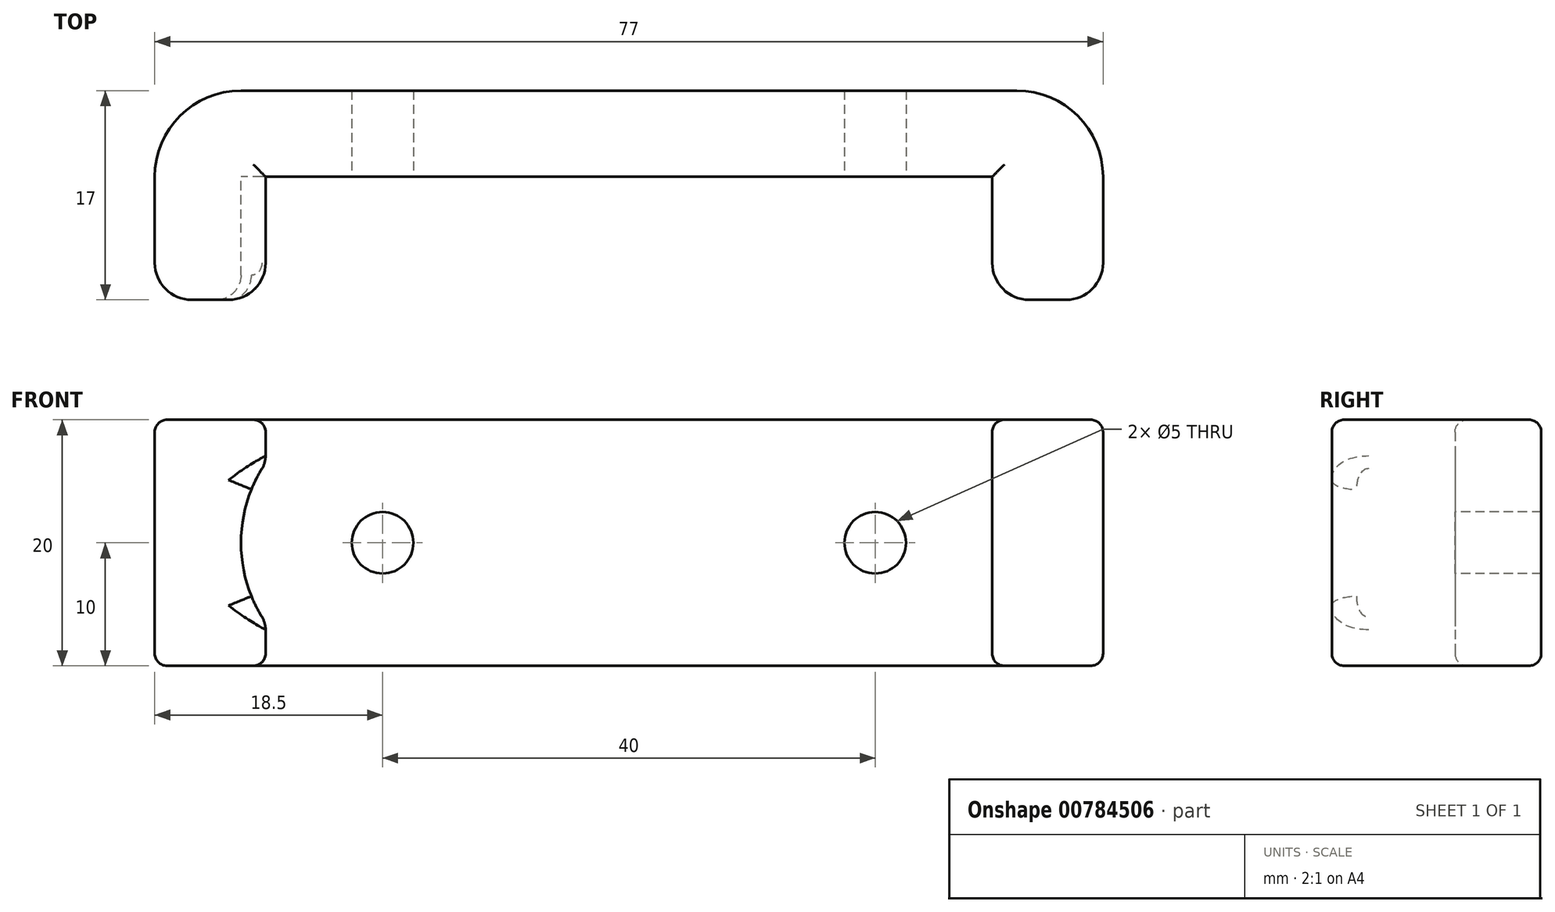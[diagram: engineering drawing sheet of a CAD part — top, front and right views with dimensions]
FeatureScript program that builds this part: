
annotation { "Feature Type Name" : "Feature", "Feature Type Description" : "" }
export const myFeature = defineFeature(function(context is Context, id is Id, definition is map)
    precondition{}
    {
        {
            var Q0;
            Q0=qCreatedBy(makeId("Top.planeOp"),FACE);
            var sketch = newSketch(context, id + "F0", { "sketchPlane" : qUnion([Q0])});
            skLineSegment(sketch, "E0.bottom", {"start": v(-31.5, 3.5) * mm, "end": v(31.5, 3.5) * mm});
            skLineSegment(sketch, "E0.top", {"start": v(-38.5, -3.5) * mm, "end": v(38.5, -3.5) * mm});
            skLineSegment(sketch, "E0.left", {"start": v(-38.5, -3.5) * mm, "end": v(-38.5, -3.5) * mm});
            skLineSegment(sketch, "E0.right", {"start": v(38.5, -3.5) * mm, "end": v(38.5, -3.5) * mm});
            skPoint(sketch, "E0.middle", {"position": v(0, 0) * mm});
            skLineSegment(sketch, "E1.bottom", {"start": v(-38.5, -3.5) * mm, "end": v(-29.5, -3.5) * mm});
            skLineSegment(sketch, "E1.top", {"start": v(-35.5, -13.5) * mm, "end": v(-32.5, -13.5) * mm});
            skLineSegment(sketch, "E1.left", {"start": v(-38.5, -3.5) * mm, "end": v(-38.5, -10.5) * mm});
            skLineSegment(sketch, "E1.right", {"start": v(-29.5, -3.5) * mm, "end": v(-29.5, -10.5) * mm});
            skLineSegment(sketch, "E2.bottom", {"start": v(38.5, -3.5) * mm, "end": v(29.5, -3.5) * mm});
            skLineSegment(sketch, "E2.top", {"start": v(35.5, -13.5) * mm, "end": v(32.5, -13.5) * mm});
            skLineSegment(sketch, "E2.left", {"start": v(38.5, -3.5) * mm, "end": v(38.5, -10.5) * mm});
            skLineSegment(sketch, "E2.right", {"start": v(29.5, -3.5) * mm, "end": v(29.5, -10.5) * mm});
            skCircle(sketch, "E3", {"center": v(0, 0) * mm, "radius": 20 * mm, "construction": true});
            skPoint(sketch, "E4.visualSharp", {"position": v(-38.5, 3.5) * mm});
            skArc(sketch, "E4.filletArc", {"start": v(-31.5, 3.5) * mm, "mid": v(-36.45, 1.45) * mm, "end": v(-38.5, -3.5) * mm});
            skPoint(sketch, "E5.visualSharp", {"position": v(38.5, 3.5) * mm});
            skArc(sketch, "E5.filletArc", {"start": v(38.5, -3.5) * mm, "mid": v(36.45, 1.45) * mm, "end": v(31.5, 3.5) * mm});
            skPoint(sketch, "E6.visualSharp", {"position": v(-38.5, -13.5) * mm});
            skArc(sketch, "E6.filletArc", {"start": v(-38.5, -10.5) * mm, "mid": v(-37.62, -12.62) * mm, "end": v(-35.5, -13.5) * mm});
            skPoint(sketch, "E7.visualSharp", {"position": v(29.5, -13.5) * mm});
            skArc(sketch, "E7.filletArc", {"start": v(29.5, -10.5) * mm, "mid": v(30.38, -12.62) * mm, "end": v(32.5, -13.5) * mm});
            skPoint(sketch, "E8.visualSharp", {"position": v(-29.5, -13.5) * mm});
            skArc(sketch, "E8.filletArc", {"start": v(-32.5, -13.5) * mm, "mid": v(-30.38, -12.62) * mm, "end": v(-29.5, -10.5) * mm});
            skPoint(sketch, "E9.visualSharp", {"position": v(38.5, -13.5) * mm});
            skArc(sketch, "E9.filletArc", {"start": v(35.5, -13.5) * mm, "mid": v(37.62, -12.62) * mm, "end": v(38.5, -10.5) * mm});
            skSolve(sketch);
        }
        {
            var Q0;
            Q0=makeQuery(id+"F0.imprint","IMPRINT",FACE,{"disambiguationData":[TD([[makeQuery(id+"F0.imprint","IMPRINT",EDGE,{"derivedFrom":sQuery(id+"F0.wireOp",EDGE,"E2.top")}),-1.0]])]});
            var Q1;
            Q1=makeQuery(id+"F0.imprint","IMPRINT",FACE,{"disambiguationData":[TD([[makeQuery(id+"F0.imprint","IMPRINT",EDGE,{"derivedFrom":sQuery(id+"F0.wireOp",EDGE,"E0.bottom")}),-1.0]])]});
            var Q2;
            Q2=makeQuery(id+"F0.imprint","IMPRINT",FACE,{"disambiguationData":[TD([[makeQuery(id+"F0.imprint","IMPRINT",EDGE,{"derivedFrom":sQuery(id+"F0.wireOp",EDGE,"E1.top")}),1.0]])]});
            extrude(context, id + "F1", {"entities" : qUnion([Q0, Q1, Q2]), "depth" : 20 * mm, "offsetDistance" : 25 * mm});
        }
        {
            var Q0;
            Q0=makeQuery(id+"F1.opExtrude","SWEPT_FACE",FACE,{"disambiguationData":[OSD([sQuery(id+"F0.wireOp",EDGE,"E0.top")])]});
            var sketch = newSketch(context, id + "F2", { "sketchPlane" : qUnion([Q0])});
            skCircle(sketch, "E10", {"center": v(0, 10) * mm, "radius": 20 * mm, "construction": true});
            skCircle(sketch, "E11", {"center": v(-20, 10) * mm, "radius": 2.5 * mm});
            skCircle(sketch, "E12", {"center": v(20, 10) * mm, "radius": 2.5 * mm});
            skCircle(sketch, "E13", {"center": v(-20, 10) * mm, "radius": 11.5 * mm});
            skCircle(sketch, "E14", {"center": v(20, 10) * mm, "radius": 11.5 * mm});
            skSolve(sketch);
        }
        {
            var Q0;
            Q0=makeQuery(id+"F2.imprint","IMPRINT",FACE,{"disambiguationData":[TD([[makeQuery(id+"F2.imprint","IMPRINT",EDGE,{"derivedFrom":sQuery(id+"F2.wireOp",EDGE,"E11")}),1.0]])]});
            var Q1;
            Q1=makeQuery(id+"F2.imprint","IMPRINT",FACE,{"disambiguationData":[TD([[makeQuery(id+"F2.imprint","IMPRINT",EDGE,{"derivedFrom":sQuery(id+"F2.wireOp",EDGE,"E12")}),1.0]])]});
            extrude(context, id + "F3", {"entities" : qUnion([Q0, Q1]), "operationType" : NewBodyOperationType.REMOVE, "oppositeDirection" : true, "depth" : 7 * mm, "offsetDistance" : 25 * mm});
        }
        {
            var Q0;
            {var subQ0=sQuery(id+"F2.wireOp",EDGE,"E13");var subQ1=makeQuery(id+"F1.opExtrude","SWEPT_EDGE",EDGE,{"disambiguationData":[OSD([sQuery(id+"F0.wireOp",EDGE,"E0.top"),sQuery(id+"F0.wireOp",EDGE,"E1.right")])]});var subQ2=makeQuery(id+"F2.imprint","INTERSECT",VERTEX,{"disambiguationData":[OD(0.0)],"derivedFrom":[subQ1,subQ0]});Q0=makeQuery(id+"F2.imprint","IMPRINT",FACE,{"disambiguationData":[TD([[makeQuery(id+"F2.imprint","IMPRINT",EDGE,{"disambiguationData":[TD([[subQ2,-1.0]])],"derivedFrom":subQ0}),1.0]])]});}
            var Q1;
            {var subQ0=sQuery(id+"F2.wireOp",EDGE,"E14");var subQ1=makeQuery(id+"F1.opExtrude","SWEPT_EDGE",EDGE,{"disambiguationData":[OSD([sQuery(id+"F0.wireOp",EDGE,"E0.top"),sQuery(id+"F0.wireOp",EDGE,"E2.right")])]});var subQ2=makeQuery(id+"F2.imprint","INTERSECT",VERTEX,{"disambiguationData":[OD(0.0)],"derivedFrom":[subQ1,subQ0]});Q1=makeQuery(id+"F2.imprint","IMPRINT",FACE,{"disambiguationData":[TD([[makeQuery(id+"F2.imprint","IMPRINT",EDGE,{"disambiguationData":[TD([[subQ2,1.0]])],"derivedFrom":subQ0}),1.0]])]});}
            var Q2;
            Q2=sQuery(id+"F2.wireOp",EDGE,"E13");
            var Q3;
            Q3=sQuery(id+"F2.wireOp",EDGE,"E14");
            extrude(context, id + "F4", {"entities" : qUnion([Q0, Q1]), "operationType" : NewBodyOperationType.REMOVE, "surfaceEntities" : qUnion([Q2, Q3]), "depth" : 25 * mm, "offsetDistance" : 25 * mm});
        }
        {
            var Q0;
            {var subQ0=sQuery(id+"F2.wireOp",EDGE,"E13");var subQ1=sQuery(id+"F0.wireOp",EDGE,"E1.right");var subQ2=sQuery(id+"F0.wireOp",EDGE,"E0.top");Q0=makeQuery(id+"F4.boolean.opBoolean","COPY",EDGE,{"derivedFrom":makeQuery(id+"F4.opExtrude","SWEPT_EDGE",EDGE,{"disambiguationData":[OSD([subQ2,subQ1,subQ0]),TDD([makeQuery(id+"F2.imprint","INTERSECT",VERTEX,{"disambiguationData":[OD(0.0)],"derivedFrom":[makeQuery(id+"F1.opExtrude","SWEPT_EDGE",EDGE,{"disambiguationData":[OSD([subQ2,subQ1])]}),subQ0]})])]})});}
            var Q1;
            {var subQ0=sQuery(id+"F2.wireOp",EDGE,"E13");var subQ1=sQuery(id+"F0.wireOp",EDGE,"E1.right");var subQ2=sQuery(id+"F0.wireOp",EDGE,"E0.top");Q1=makeQuery(id+"F4.boolean.opBoolean","COPY",EDGE,{"derivedFrom":makeQuery(id+"F4.opExtrude","SWEPT_EDGE",EDGE,{"disambiguationData":[OSD([subQ2,subQ1,subQ0]),TDD([makeQuery(id+"F2.imprint","INTERSECT",VERTEX,{"disambiguationData":[OD(1.0)],"derivedFrom":[makeQuery(id+"F1.opExtrude","SWEPT_EDGE",EDGE,{"disambiguationData":[OSD([subQ2,subQ1])]}),subQ0]})])]})});}
            var Q2;
            {var subQ0=sQuery(id+"F2.wireOp",EDGE,"E14");var subQ1=sQuery(id+"F0.wireOp",EDGE,"E2.right");var subQ2=sQuery(id+"F0.wireOp",EDGE,"E0.top");Q2=makeQuery(id+"F4.boolean.opBoolean","COPY",EDGE,{"derivedFrom":makeQuery(id+"F4.opExtrude","SWEPT_EDGE",EDGE,{"disambiguationData":[OSD([subQ2,subQ1,subQ0]),TDD([makeQuery(id+"F2.imprint","INTERSECT",VERTEX,{"disambiguationData":[OD(0.0)],"derivedFrom":[makeQuery(id+"F1.opExtrude","SWEPT_EDGE",EDGE,{"disambiguationData":[OSD([subQ2,subQ1])]}),subQ0]})])]})});}
            var Q3;
            {var subQ0=sQuery(id+"F2.wireOp",EDGE,"E14");var subQ1=sQuery(id+"F0.wireOp",EDGE,"E2.right");var subQ2=sQuery(id+"F0.wireOp",EDGE,"E0.top");Q3=makeQuery(id+"F4.boolean.opBoolean","COPY",EDGE,{"derivedFrom":makeQuery(id+"F4.opExtrude","SWEPT_EDGE",EDGE,{"disambiguationData":[OSD([subQ2,subQ1,subQ0]),TDD([makeQuery(id+"F2.imprint","INTERSECT",VERTEX,{"disambiguationData":[OD(1.0)],"derivedFrom":[makeQuery(id+"F1.opExtrude","SWEPT_EDGE",EDGE,{"disambiguationData":[OSD([subQ2,subQ1])]}),subQ0]})])]})});}
            var Q4;
            Q4=makeQuery(id+"F4.boolean.opBoolean","INTERSECT",EDGE,{"derivedFrom":[makeQuery(id+"F1.opExtrude","SWEPT_FACE",FACE,{"disambiguationData":[OSD([sQuery(id+"F0.wireOp",EDGE,"E7.filletArc")])]}),makeQuery(id+"F4.opExtrude","SWEPT_FACE",FACE,{"disambiguationData":[OSD([sQuery(id+"F2.wireOp",EDGE,"E14")])]})]});
            fillet(context, id + "F5", {"entities" : qUnion([Q0, Q1, Q2, Q3, Q4]), "radius" : 2 * mm, "tangentPropagation" : true, "allowEdgeOverflow" : false});
        }
        {
            var Q0;
            Q0=makeQuery(id+"F1.opExtrude","CAP_FACE",FACE,{"disambiguationData":[OSD([sQuery(id+"F0.wireOp",EDGE,"E0.bottom"),sQuery(id+"F0.wireOp",EDGE,"E0.top"),sQuery(id+"F0.wireOp",EDGE,"E1.top"),sQuery(id+"F0.wireOp",EDGE,"E1.left"),sQuery(id+"F0.wireOp",EDGE,"E1.right"),sQuery(id+"F0.wireOp",EDGE,"E2.top"),sQuery(id+"F0.wireOp",EDGE,"E2.left"),sQuery(id+"F0.wireOp",EDGE,"E2.right"),sQuery(id+"F0.wireOp",EDGE,"E4.filletArc"),sQuery(id+"F0.wireOp",EDGE,"E5.filletArc"),sQuery(id+"F0.wireOp",EDGE,"E6.filletArc"),sQuery(id+"F0.wireOp",EDGE,"E7.filletArc"),sQuery(id+"F0.wireOp",EDGE,"E8.filletArc"),sQuery(id+"F0.wireOp",EDGE,"E9.filletArc")])],"isStart":true});
            var Q1;
            Q1=makeQuery(id+"F1.opExtrude","CAP_FACE",FACE,{"disambiguationData":[OSD([sQuery(id+"F0.wireOp",EDGE,"E0.bottom"),sQuery(id+"F0.wireOp",EDGE,"E0.top"),sQuery(id+"F0.wireOp",EDGE,"E1.top"),sQuery(id+"F0.wireOp",EDGE,"E1.left"),sQuery(id+"F0.wireOp",EDGE,"E1.right"),sQuery(id+"F0.wireOp",EDGE,"E2.top"),sQuery(id+"F0.wireOp",EDGE,"E2.left"),sQuery(id+"F0.wireOp",EDGE,"E2.right"),sQuery(id+"F0.wireOp",EDGE,"E4.filletArc"),sQuery(id+"F0.wireOp",EDGE,"E5.filletArc"),sQuery(id+"F0.wireOp",EDGE,"E6.filletArc"),sQuery(id+"F0.wireOp",EDGE,"E7.filletArc"),sQuery(id+"F0.wireOp",EDGE,"E8.filletArc"),sQuery(id+"F0.wireOp",EDGE,"E9.filletArc")])],"isStart":false});
            fillet(context, id + "F6", {"entities" : qUnion([Q0, Q1]), "radius" : 1 * mm, "tangentPropagation" : true, "allowEdgeOverflow" : false});
        }
    });
